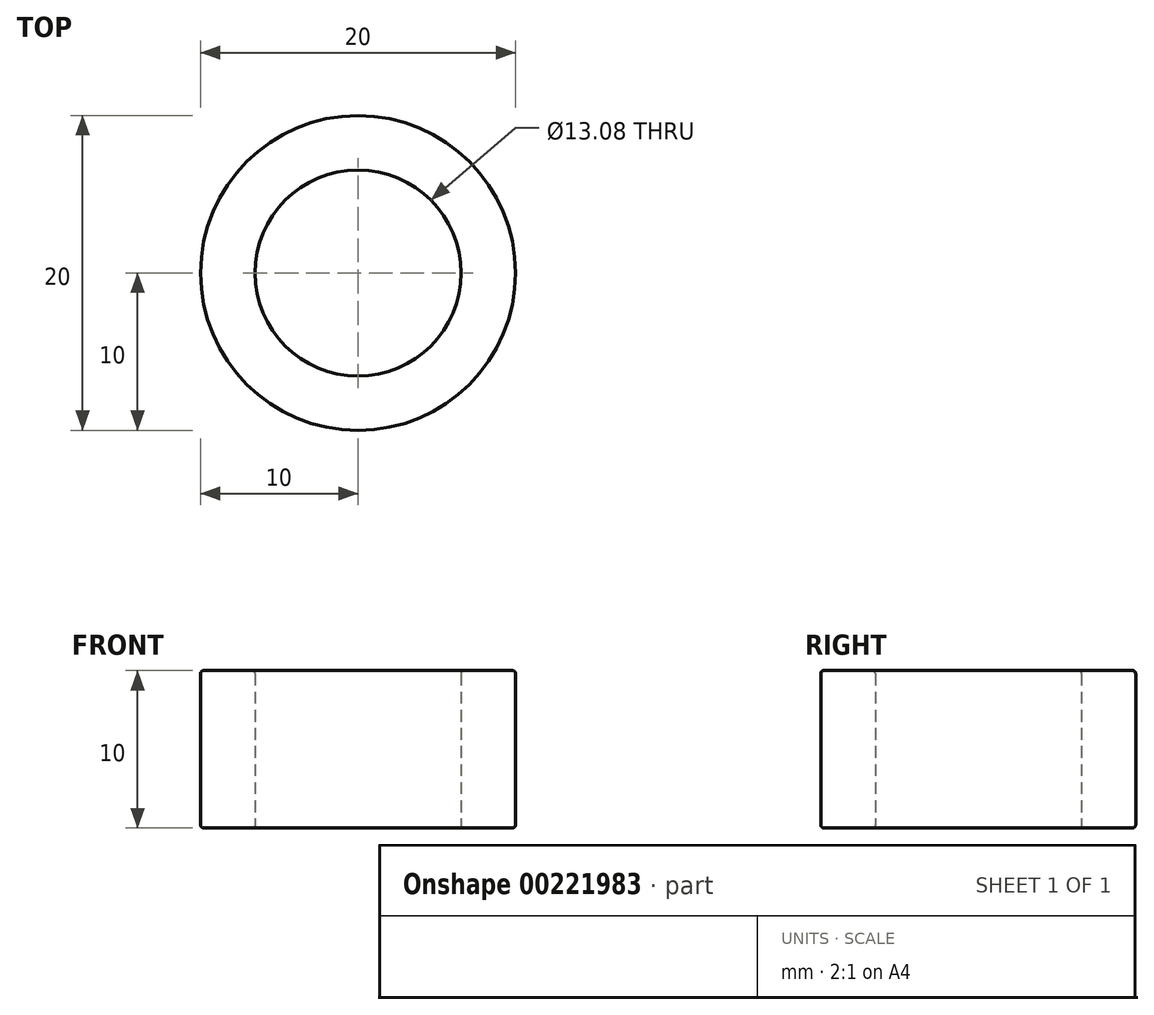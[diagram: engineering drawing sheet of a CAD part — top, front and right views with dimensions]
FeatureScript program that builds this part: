
annotation { "Feature Type Name" : "Feature", "Feature Type Description" : "" }
export const myFeature = defineFeature(function(context is Context, id is Id, definition is map)
    precondition{}
    {
        {
            var Q0;
            Q0=qCreatedBy(makeId("Top.planeOp"),FACE);
            var sketch = newSketch(context, id + "F0", { "sketchPlane" : qUnion([Q0])});
            skCircle(sketch, "E0", {"center": v(0, 0) * mm, "radius": 10 * mm});
            skCircle(sketch, "E1", {"center": v(0, 0) * mm, "radius": 6.54 * mm});
            skSolve(sketch);
        }
        {
            var Q0;
            Q0 = qSketchRegion(id + "F0", true);
            extrude(context, id + "F1", {"entities" : qUnion([Q0]), "depth" : 10 * mm});
        }
        {
            var Q0;
            Q0=makeQuery(id+"F1.opExtrude","CAP_EDGE",EDGE,{"disambiguationData":[OSD([sQuery(id+"F0.wireOp",EDGE,"E0")])],"isStart":false});
            var Q1;
            Q1=makeQuery(id+"F1.opExtrude","CAP_EDGE",EDGE,{"disambiguationData":[OSD([sQuery(id+"F0.wireOp",EDGE,"E1")])],"isStart":false});
            var Q2;
            Q2=makeQuery(id+"F1.opExtrude","CAP_EDGE",EDGE,{"disambiguationData":[OSD([sQuery(id+"F0.wireOp",EDGE,"E0")])],"isStart":true});
            var Q3;
            Q3=makeQuery(id+"F1.opExtrude","CAP_EDGE",EDGE,{"disambiguationData":[OSD([sQuery(id+"F0.wireOp",EDGE,"E1")])],"isStart":true});
            fillet(context, id + "F2", {"entities" : qUnion([Q0, Q1, Q2, Q3]), "radius" : .2 * mm, "tangentPropagation" : true, "allowEdgeOverflow" : false});
        }
    });
